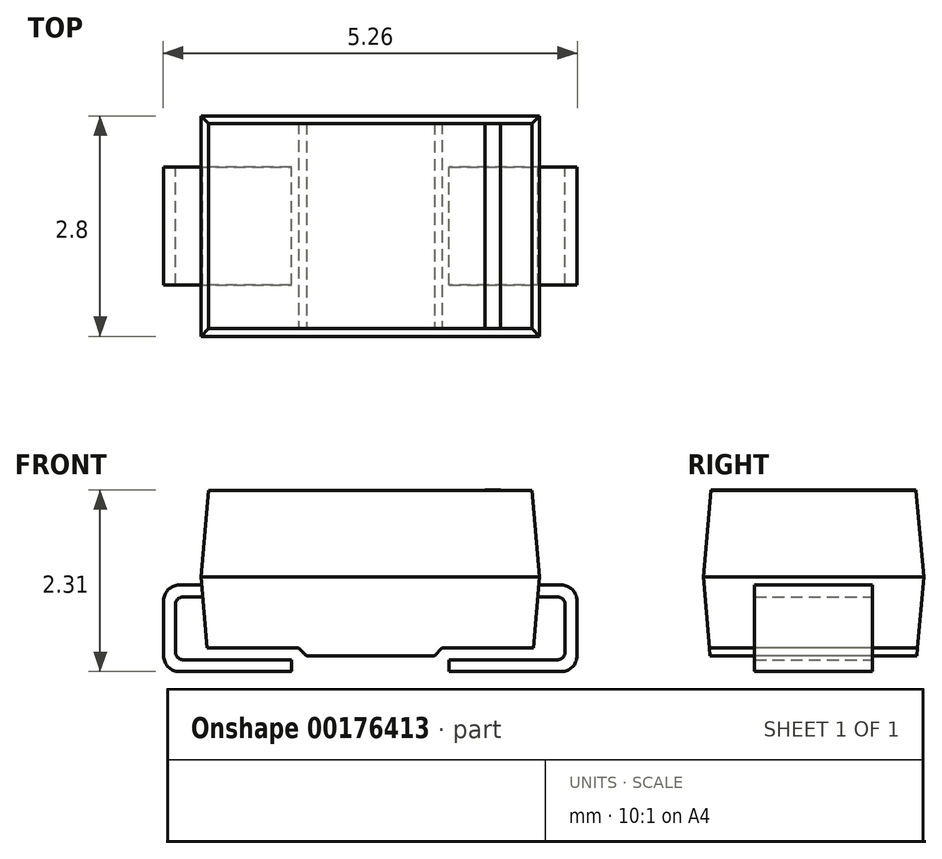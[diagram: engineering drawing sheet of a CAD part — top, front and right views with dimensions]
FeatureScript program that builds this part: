
annotation { "Feature Type Name" : "Feature", "Feature Type Description" : "" }
export const myFeature = defineFeature(function(context is Context, id is Id, definition is map)
    precondition{}
    {
        {
            var Q0;
            Q0=qCreatedBy(makeId("Top.planeOp"),FACE);
            var sketch = newSketch(context, id + "F0", { "sketchPlane" : qUnion([Q0])});
            skLineSegment(sketch, "E0.bottom", {"start": v(2.15, 1.4) * mm, "end": v(-2.15, 1.4) * mm});
            skLineSegment(sketch, "E0.top", {"start": v(2.15, -1.4) * mm, "end": v(-2.15, -1.4) * mm});
            skLineSegment(sketch, "E0.left", {"start": v(2.15, 1.4) * mm, "end": v(2.15, -1.4) * mm});
            skLineSegment(sketch, "E0.right", {"start": v(-2.15, 1.4) * mm, "end": v(-2.15, -1.4) * mm});
            skPoint(sketch, "E0.middle", {"position": v(0, 0) * mm});
            skSolve(sketch);
        }
        {
            var Q0;
            Q0 = qSketchRegion(id + "F0", true);
            extrude(context, id + "F1", {"entities" : qUnion([Q0]), "depth" : 1.1 * mm, "hasDraft" : true, "draftAngle" : 5 * degree, "draftPullDirection" : true});
        }
        {
            var Q0;
            Q0 = qSketchRegion(id + "F0", true);
            extrude(context, id + "F2", {"entities" : qUnion([Q0]), "operationType" : NewBodyOperationType.ADD, "oppositeDirection" : true, "depth" : 1 * mm, "hasDraft" : true, "draftAngle" : 5 * degree, "draftPullDirection" : true});
        }
        {
            var Q0;
            Q0=qCreatedBy(makeId("Front.planeOp"),FACE);
            var sketch = newSketch(context, id + "F3", { "sketchPlane" : qUnion([Q0])});
            skLineSegment(sketch, "E1", {"start": v(-2.14, -0.1) * mm, "end": v(-2.62, -0.1) * mm});
            skLineSegment(sketch, "E2", {"start": v(-2.62, -0.1) * mm, "end": v(-2.62, -1.2) * mm});
            skLineSegment(sketch, "E3", {"start": v(-2.62, -1.2) * mm, "end": v(-1, -1.2) * mm});
            skLineSegment(sketch, "E4", {"start": v(-1, -1.2) * mm, "end": v(-1, -1.05) * mm});
            skLineSegment(sketch, "E5", {"start": v(-1, -1.05) * mm, "end": v(-2.47, -1.05) * mm});
            skLineSegment(sketch, "E6", {"start": v(-2.47, -1.05) * mm, "end": v(-2.47, -0.25) * mm});
            skLineSegment(sketch, "E7", {"start": v(-2.47, -0.25) * mm, "end": v(-2.13, -0.25) * mm});
            skLineSegment(sketch, "E8", {"start": v(-2.13, -0.25) * mm, "end": v(-2.14, -0.1) * mm});
            skLineSegment(sketch, "E9", {"start": v(-2.47, -0.25) * mm, "end": v(-2.47, -0.1) * mm, "construction": true});
            skLineSegment(sketch, "E10", {"start": v(-2.47, -0.25) * mm, "end": v(-2.62, -0.25) * mm, "construction": true});
            skLineSegment(sketch, "E11", {"start": v(0, 0) * mm, "end": v(0, 1.1) * mm, "construction": true});
            skLineSegment(sketch, "E12.MirrorCS", {"start": v(2.13, -0.25) * mm, "end": v(2.14, -0.1) * mm});
            skLineSegment(sketch, "E13.MirrorCS", {"start": v(1, -1.2) * mm, "end": v(1, -1.05) * mm});
            skLineSegment(sketch, "E14.MirrorCS", {"start": v(2.47, -0.25) * mm, "end": v(2.47, -0.1) * mm, "construction": true});
            skLineSegment(sketch, "E15.MirrorCS", {"start": v(2.47, -0.25) * mm, "end": v(2.62, -0.25) * mm, "construction": true});
            skLineSegment(sketch, "E16.MirrorCS", {"start": v(2.47, -0.25) * mm, "end": v(2.13, -0.25) * mm});
            skLineSegment(sketch, "E17.MirrorCS", {"start": v(2.47, -1.05) * mm, "end": v(2.47, -0.25) * mm});
            skLineSegment(sketch, "E18.MirrorCS", {"start": v(1, -1.05) * mm, "end": v(2.47, -1.05) * mm});
            skLineSegment(sketch, "E19.MirrorCS", {"start": v(2.14, -0.1) * mm, "end": v(2.62, -0.1) * mm});
            skLineSegment(sketch, "E20.MirrorCS", {"start": v(2.62, -1.2) * mm, "end": v(1, -1.2) * mm});
            skLineSegment(sketch, "E21.MirrorCS", {"start": v(2.62, -0.1) * mm, "end": v(2.62, -1.2) * mm});
            skSolve(sketch);
        }
        {
            var Q0;
            Q0 = qSketchRegion(id + "F3", true);
            extrude(context, id + "F4", {"entities" : qUnion([Q0]), "endBound" : BoundingType.SYMMETRIC, "depth" : 1.5 * mm});
        }
        {
            var Q0;
            Q0=makeQuery(id+"F4.opExtrude","SWEPT_EDGE",EDGE,{"disambiguationData":[OSD([sQuery(id+"F3.wireOp",EDGE,"E1"),sQuery(id+"F3.wireOp",EDGE,"E2")])]});
            var Q1;
            Q1=makeQuery(id+"F4.opExtrude","SWEPT_EDGE",EDGE,{"disambiguationData":[OSD([sQuery(id+"F3.wireOp",EDGE,"E19.MirrorCS"),sQuery(id+"F3.wireOp",EDGE,"E21.MirrorCS")])]});
            var Q2;
            Q2=makeQuery(id+"F4.opExtrude","SWEPT_EDGE",EDGE,{"disambiguationData":[OSD([sQuery(id+"F3.wireOp",EDGE,"E2"),sQuery(id+"F3.wireOp",EDGE,"E3")])]});
            var Q3;
            Q3=makeQuery(id+"F4.opExtrude","SWEPT_EDGE",EDGE,{"disambiguationData":[OSD([sQuery(id+"F3.wireOp",EDGE,"E20.MirrorCS"),sQuery(id+"F3.wireOp",EDGE,"E21.MirrorCS")])]});
            fillet(context, id + "F5", {"entities" : qUnion([Q0, Q1, Q2, Q3]), "radius" : 0.2 * mm, "tangentPropagation" : true, "allowEdgeOverflow" : false});
        }
        {
            var Q0;
            Q0=makeQuery(id+"F4.opExtrude","SWEPT_EDGE",EDGE,{"disambiguationData":[OSD([sQuery(id+"F3.wireOp",EDGE,"E6"),sQuery(id+"F3.wireOp",EDGE,"E7")])]});
            var Q1;
            Q1=makeQuery(id+"F4.opExtrude","SWEPT_EDGE",EDGE,{"disambiguationData":[OSD([sQuery(id+"F3.wireOp",EDGE,"E17.MirrorCS"),sQuery(id+"F3.wireOp",EDGE,"E18.MirrorCS")])]});
            var Q2;
            Q2=makeQuery(id+"F4.opExtrude","SWEPT_EDGE",EDGE,{"disambiguationData":[OSD([sQuery(id+"F3.wireOp",EDGE,"E5"),sQuery(id+"F3.wireOp",EDGE,"E6")])]});
            var Q3;
            Q3=makeQuery(id+"F4.opExtrude","SWEPT_EDGE",EDGE,{"disambiguationData":[OSD([sQuery(id+"F3.wireOp",EDGE,"E16.MirrorCS"),sQuery(id+"F3.wireOp",EDGE,"E17.MirrorCS")])]});
            fillet(context, id + "F6", {"entities" : qUnion([Q0, Q1, Q2, Q3]), "radius" : 0.1 * mm, "tangentPropagation" : true, "allowEdgeOverflow" : false});
        }
        {
            var Q0;
            Q0=qCreatedBy(makeId("Front.planeOp"),FACE);
            var sketch = newSketch(context, id + "F7", { "sketchPlane" : qUnion([Q0])});
            skLineSegment(sketch, "E22", {"start": v(2.07, -0.9) * mm, "end": v(0.91, -0.9) * mm});
            skLineSegment(sketch, "E23", {"start": v(0.91, -0.9) * mm, "end": v(0.81, -1) * mm});
            skLineSegment(sketch, "E24", {"start": v(0.81, -1) * mm, "end": v(2.06, -1) * mm});
            skLineSegment(sketch, "E25", {"start": v(2.06, -1) * mm, "end": v(2.07, -0.9) * mm});
            skLineSegment(sketch, "E26", {"start": v(0, 0) * mm, "end": v(0, -1.2) * mm, "construction": true});
            skLineSegment(sketch, "E27.MirrorCS", {"start": v(-2.06, -1) * mm, "end": v(-2.07, -0.9) * mm});
            skLineSegment(sketch, "E28.MirrorCS", {"start": v(-0.81, -1) * mm, "end": v(-2.06, -1) * mm});
            skLineSegment(sketch, "E29.MirrorCS", {"start": v(-0.91, -0.9) * mm, "end": v(-0.81, -1) * mm});
            skLineSegment(sketch, "E30.MirrorCS", {"start": v(-2.07, -0.9) * mm, "end": v(-0.91, -0.9) * mm});
            skSolve(sketch);
        }
        {
            var Q0;
            Q0 = qSketchRegion(id + "F7", true);
            extrude(context, id + "F8", {"entities" : qUnion([Q0]), "operationType" : NewBodyOperationType.REMOVE, "endBound" : BoundingType.SYMMETRIC, "oppositeDirection" : true, "depth" : 25 * mm});
        }
        {
            var Q0;
            Q0=makeQuery(id+"F1.opExtrude","CAP_FACE",FACE,{"disambiguationData":[OSD([sQuery(id+"F0.wireOp",EDGE,"E0.bottom"),sQuery(id+"F0.wireOp",EDGE,"E0.top"),sQuery(id+"F0.wireOp",EDGE,"E0.left"),sQuery(id+"F0.wireOp",EDGE,"E0.right")])],"isStart":false});
            var sketch = newSketch(context, id + "F9", { "sketchPlane" : qUnion([Q0])});
            skLineSegment(sketch, "E31.bottom", {"start": v(1.65, -1.3) * mm, "end": v(1.45, -1.3) * mm});
            skLineSegment(sketch, "E31.top", {"start": v(1.65, 1.3) * mm, "end": v(1.45, 1.3) * mm});
            skLineSegment(sketch, "E31.left", {"start": v(1.65, -1.3) * mm, "end": v(1.65, 1.3) * mm});
            skLineSegment(sketch, "E31.right", {"start": v(1.45, -1.3) * mm, "end": v(1.45, 1.3) * mm});
            skSolve(sketch);
        }
        {
            var Q0;
            Q0 = qSketchRegion(id + "F9", true);
            extrude(context, id + "F10", {"entities" : qUnion([Q0]), "depth" : 0.01 * mm});
        }
    });
